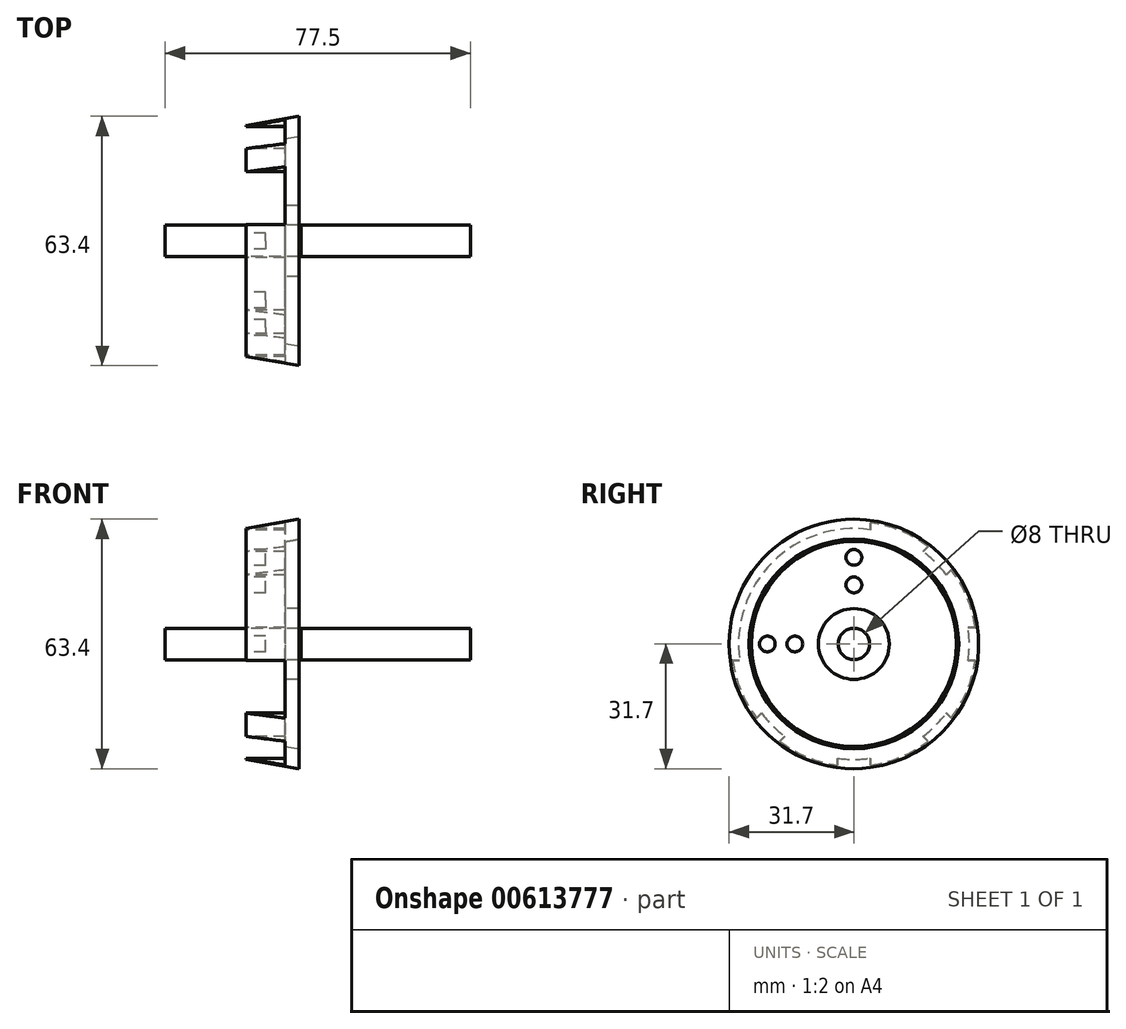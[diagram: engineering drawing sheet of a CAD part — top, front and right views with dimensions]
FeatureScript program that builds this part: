
annotation { "Feature Type Name" : "Feature", "Feature Type Description" : "" }
export const myFeature = defineFeature(function(context is Context, id is Id, definition is map)
    precondition{}
    {
        {
            var Q0;
            Q0=qCreatedBy(makeId("Front.planeOp"),FACE);
            var sketch = newSketch(context, id + "F0", { "sketchPlane" : qUnion([Q0])});
            skLineSegment(sketch, "E0", {"start": v(0, 0) * mm, "end": v(43, 0) * mm});
            skLineSegment(sketch, "E1", {"start": v(43, 0) * mm, "end": v(43, 14.5) * mm});
            skLineSegment(sketch, "E2", {"start": v(43, 14.5) * mm, "end": v(42, 14.5) * mm});
            skLineSegment(sketch, "E3", {"start": v(42, 14.5) * mm, "end": v(42, 31.7) * mm});
            skLineSegment(sketch, "E4", {"start": v(42, 31.7) * mm, "end": v(0, 31.7) * mm});
            skLineSegment(sketch, "E5", {"start": v(0, 31.7) * mm, "end": v(0, 0) * mm});
            skLineSegment(sketch, "E6", {"start": v(-0.5, 0) * mm, "end": v(-0.5, 31.7) * mm});
            skLineSegment(sketch, "E7", {"start": v(-0.5, 31.7) * mm, "end": v(-14, 29.32) * mm});
            skLineSegment(sketch, "E8", {"start": v(-14, 29.32) * mm, "end": v(-14, 0) * mm});
            skLineSegment(sketch, "E9", {"start": v(-14, 0) * mm, "end": v(-0.5, 0) * mm});
            skLineSegment(sketch, "E10", {"start": v(-34.5, 0) * mm, "end": v(43, 0) * mm});
            skLineSegment(sketch, "E11", {"start": v(-14, 29.32) * mm, "end": v(-14, 31.7) * mm});
            skLineSegment(sketch, "E12", {"start": v(-14, 31.7) * mm, "end": v(-0.5, 31.7) * mm});
            skLineSegment(sketch, "E13", {"start": v(-0.5, 31.7) * mm, "end": v(-0.5, 31.7) * mm});
            skLineSegment(sketch, "E14", {"start": v(-34.5, 0) * mm, "end": v(-34.5, 4) * mm});
            skLineSegment(sketch, "E15", {"start": v(-34.5, 4) * mm, "end": v(43, 4) * mm});
            skPoint(sketch, "E15.endSnap0", {"position": v(43, 7.25) * mm});
            skLineSegment(sketch, "E16", {"start": v(43, 4) * mm, "end": v(43, 0) * mm});
            skSolve(sketch);
        }
        {
            var Q0;
            {var subQ0=sQuery(id+"F0.wireOp",EDGE,"E7");Q0=makeQuery(id+"F0.imprint","IMPRINT",FACE,{"disambiguationData":[TD([[makeQuery(id+"F0.imprint","IMPRINT",EDGE,{"derivedFrom":subQ0}),1.0]])]});}
            var Q1;
            Q1=sQuery(id+"F0.wireOp",EDGE,"E10");
            revolve(context, id + "F1", {"entities" : qUnion([Q0]), "axis" : qUnion([Q1]), "revolveType" : RevolveType.FULL});
        }
        {
            var Q0;
            {var subQ1=sQuery(id+"F0.wireOp",EDGE,"E1");Q0=makeQuery(id+"F0.imprint","IMPRINT",FACE,{"disambiguationData":[TD([[makeQuery(id+"F0.imprint","IMPRINT",EDGE,{"derivedFrom":subQ1}),1.0]])]});}
            var Q1;
            {var subQ5=sQuery(id+"F0.wireOp",EDGE,"E14");Q1=makeQuery(id+"F0.imprint","IMPRINT",FACE,{"disambiguationData":[TD([[makeQuery(id+"F0.imprint","IMPRINT",EDGE,{"derivedFrom":subQ5}),-1.0]])]});}
            var Q2;
            {var subQ0=sQuery(id+"F0.wireOp",EDGE,"E10");var subQ1=sQuery(id+"F0.wireOp",EDGE,"E6");var subQ2=makeQuery(id+"F0.imprint","INTERSECT",VERTEX,{"derivedFrom":[subQ1,subQ0]});Q2=makeQuery(id+"F0.imprint","IMPRINT",FACE,{"disambiguationData":[TD([[makeQuery(id+"F0.imprint","IMPRINT",EDGE,{"disambiguationData":[TD([[subQ2,-1.0]])],"derivedFrom":subQ1}),1.0]])]});}
            var Q3;
            {var subQ5=sQuery(id+"F0.wireOp",EDGE,"E16");Q3=makeQuery(id+"F0.imprint","IMPRINT",FACE,{"disambiguationData":[TD([[makeQuery(id+"F0.imprint","IMPRINT",EDGE,{"derivedFrom":subQ5}),-1.0]])]});}
            var Q4;
            Q4=sQuery(id+"F0.wireOp",EDGE,"E10");
            revolve(context, id + "F2", {"entities" : qUnion([Q0, Q1, Q2, Q3]), "axis" : qUnion([Q4]), "revolveType" : RevolveType.FULL});
        }
        {
            var Q0;
            Q0=makeQuery(id+"F2.opRevolve","SWEPT_FACE",FACE,{"disambiguationData":[OSD([sQuery(id+"F0.wireOp",EDGE,"E1"),sQuery(id+"F0.wireOp",EDGE,"E16")])]});
            var sketch = newSketch(context, id + "F3", { "sketchPlane" : qUnion([Q0])});
            skCircle(sketch, "E17", {"center": v(0, 11) * mm, "radius": 2 * mm});
            skLineSegment(sketch, "E18", {"start": v(0, 31.85) * mm, "end": v(0, -39.83) * mm, "construction": true});
            skCircle(sketch, "E19.1.0", {"center": v(-11, 0) * mm, "radius": 2 * mm});
            skCircle(sketch, "E19.2.0", {"center": v(0, -11) * mm, "radius": 2 * mm});
            skCircle(sketch, "E19.3.0", {"center": v(11, 0) * mm, "radius": 2 * mm});
            skPoint(sketch, "E19.center", {"position": v(0, 0) * mm});
            skSolve(sketch);
        }
        {
            var Q0;
            Q0=makeQuery(id+"F3.imprint","IMPRINT",FACE,{"disambiguationData":[TD([[makeQuery(id+"F3.imprint","IMPRINT",EDGE,{"derivedFrom":sQuery(id+"F3.wireOp",EDGE,"E17")}),1.0]])]});
            var Q1;
            Q1=makeQuery(id+"F3.imprint","IMPRINT",FACE,{"disambiguationData":[TD([[makeQuery(id+"F3.imprint","IMPRINT",EDGE,{"derivedFrom":sQuery(id+"F3.wireOp",EDGE,"E19.1.0")}),1.0]])]});
            var Q2;
            Q2=makeQuery(id+"F3.imprint","IMPRINT",FACE,{"disambiguationData":[TD([[makeQuery(id+"F3.imprint","IMPRINT",EDGE,{"derivedFrom":sQuery(id+"F3.wireOp",EDGE,"E19.2.0")}),1.0]])]});
            var Q3;
            Q3=makeQuery(id+"F3.imprint","IMPRINT",FACE,{"disambiguationData":[TD([[makeQuery(id+"F3.imprint","IMPRINT",EDGE,{"derivedFrom":sQuery(id+"F3.wireOp",EDGE,"E19.3.0")}),1.0]])]});
            extrude(context, id + "F4", {"entities" : qUnion([Q0, Q1, Q2, Q3]), "operationType" : NewBodyOperationType.REMOVE, "oppositeDirection" : true, "depth" : 10 * mm, "offsetDistance" : 25 * mm});
        }
        {
            var Q0;
            Q0=makeQuery(id+"F1.opRevolve","SWEPT_FACE",FACE,{"disambiguationData":[OSD([sQuery(id+"F0.wireOp",EDGE,"E8")])]});
            var sketch = newSketch(context, id + "F5", { "sketchPlane" : qUnion([Q0])});
            skCircle(sketch, "E20", {"center": v(0, 0) * mm, "radius": 15 * mm});
            skCircle(sketch, "E21", {"center": v(0, 15) * mm, "radius": 2 * mm});
            skPoint(sketch, "E22.center.orphan", {"position": v(0, 22) * mm});
            skCircle(sketch, "E23", {"center": v(0, 0) * mm, "radius": 22 * mm});
            skCircle(sketch, "E24", {"center": v(0, 22) * mm, "radius": 2 * mm});
            skCircle(sketch, "E25.1.0", {"center": v(-22, 0) * mm, "radius": 2 * mm});
            skCircle(sketch, "E25.1.1", {"center": v(-15, 0) * mm, "radius": 2 * mm});
            skCircle(sketch, "E25.2.0", {"center": v(0, -22) * mm, "radius": 2 * mm});
            skCircle(sketch, "E25.2.1", {"center": v(0, -15) * mm, "radius": 2 * mm});
            skCircle(sketch, "E25.3.0", {"center": v(22, 0) * mm, "radius": 2 * mm});
            skCircle(sketch, "E25.3.1", {"center": v(15, 0) * mm, "radius": 2 * mm});
            skSolve(sketch);
        }
        {
            var Q0;
            Q0=makeQuery(id+"F1.opRevolve","SWEPT_FACE",FACE,{"disambiguationData":[OSD([sQuery(id+"F0.wireOp",EDGE,"E6")])]});
            shell(context, id + "F6", {"entities" : qUnion([Q0]), "thickness" : 5 * mm});
        }
        {
            var Q0;
            {var subQ0=sQuery(id+"F5.wireOp",EDGE,"E25.1.0");var subQ1=sQuery(id+"F5.wireOp",EDGE,"E23");var subQ2=makeQuery(id+"F5.imprint","INTERSECT",VERTEX,{"disambiguationData":[OD(0.0)],"derivedFrom":[subQ1,subQ0]});Q0=makeQuery(id+"F5.imprint","IMPRINT",FACE,{"disambiguationData":[TD([[makeQuery(id+"F5.imprint","IMPRINT",EDGE,{"disambiguationData":[TD([[subQ2,-1.0]])],"derivedFrom":subQ1}),-1.0]])]});}
            var Q1;
            {var subQ0=sQuery(id+"F5.wireOp",EDGE,"E25.1.0");var subQ1=sQuery(id+"F5.wireOp",EDGE,"E23");var subQ2=makeQuery(id+"F5.imprint","INTERSECT",VERTEX,{"disambiguationData":[OD(0.0)],"derivedFrom":[subQ1,subQ0]});Q1=makeQuery(id+"F5.imprint","IMPRINT",FACE,{"disambiguationData":[TD([[makeQuery(id+"F5.imprint","IMPRINT",EDGE,{"disambiguationData":[TD([[subQ2,-1.0]])],"derivedFrom":subQ1}),1.0]])]});}
            var Q2;
            {var subQ0=sQuery(id+"F5.wireOp",EDGE,"E25.1.1");var subQ1=sQuery(id+"F5.wireOp",EDGE,"E20");var subQ2=makeQuery(id+"F5.imprint","INTERSECT",VERTEX,{"disambiguationData":[OD(0.0)],"derivedFrom":[subQ1,subQ0]});Q2=makeQuery(id+"F5.imprint","IMPRINT",FACE,{"disambiguationData":[TD([[makeQuery(id+"F5.imprint","IMPRINT",EDGE,{"disambiguationData":[TD([[subQ2,-1.0]])],"derivedFrom":subQ1}),1.0]])]});}
            var Q3;
            {var subQ0=sQuery(id+"F5.wireOp",EDGE,"E25.1.1");var subQ1=sQuery(id+"F5.wireOp",EDGE,"E20");var subQ2=makeQuery(id+"F5.imprint","INTERSECT",VERTEX,{"disambiguationData":[OD(0.0)],"derivedFrom":[subQ1,subQ0]});Q3=makeQuery(id+"F5.imprint","IMPRINT",FACE,{"disambiguationData":[TD([[makeQuery(id+"F5.imprint","IMPRINT",EDGE,{"disambiguationData":[TD([[subQ2,-1.0]])],"derivedFrom":subQ1}),-1.0]])]});}
            var Q4;
            {var subQ0=sQuery(id+"F5.wireOp",EDGE,"E24");var subQ1=sQuery(id+"F5.wireOp",EDGE,"E23");var subQ2=makeQuery(id+"F5.imprint","INTERSECT",VERTEX,{"disambiguationData":[OD(0.0)],"derivedFrom":[subQ1,subQ0]});Q4=makeQuery(id+"F5.imprint","IMPRINT",FACE,{"disambiguationData":[TD([[makeQuery(id+"F5.imprint","IMPRINT",EDGE,{"disambiguationData":[TD([[subQ2,-1.0]])],"derivedFrom":subQ1}),1.0]])]});}
            var Q5;
            {var subQ0=sQuery(id+"F5.wireOp",EDGE,"E24");var subQ1=sQuery(id+"F5.wireOp",EDGE,"E23");var subQ2=makeQuery(id+"F5.imprint","INTERSECT",VERTEX,{"disambiguationData":[OD(0.0)],"derivedFrom":[subQ1,subQ0]});Q5=makeQuery(id+"F5.imprint","IMPRINT",FACE,{"disambiguationData":[TD([[makeQuery(id+"F5.imprint","IMPRINT",EDGE,{"disambiguationData":[TD([[subQ2,-1.0]])],"derivedFrom":subQ1}),-1.0]])]});}
            var Q6;
            {var subQ0=sQuery(id+"F5.wireOp",EDGE,"E21");var subQ1=sQuery(id+"F5.wireOp",EDGE,"E20");var subQ2=makeQuery(id+"F5.imprint","INTERSECT",VERTEX,{"disambiguationData":[OD(0.0)],"derivedFrom":[subQ1,subQ0]});Q6=makeQuery(id+"F5.imprint","IMPRINT",FACE,{"disambiguationData":[TD([[makeQuery(id+"F5.imprint","IMPRINT",EDGE,{"disambiguationData":[TD([[subQ2,-1.0]])],"derivedFrom":subQ1}),-1.0]])]});}
            var Q7;
            {var subQ0=sQuery(id+"F5.wireOp",EDGE,"E21");var subQ1=sQuery(id+"F5.wireOp",EDGE,"E20");var subQ2=makeQuery(id+"F5.imprint","INTERSECT",VERTEX,{"disambiguationData":[OD(0.0)],"derivedFrom":[subQ1,subQ0]});Q7=makeQuery(id+"F5.imprint","IMPRINT",FACE,{"disambiguationData":[TD([[makeQuery(id+"F5.imprint","IMPRINT",EDGE,{"disambiguationData":[TD([[subQ2,-1.0]])],"derivedFrom":subQ1}),1.0]])]});}
            var Q8;
            {var subQ0=sQuery(id+"F5.wireOp",EDGE,"E25.3.1");var subQ1=sQuery(id+"F5.wireOp",EDGE,"E20");var subQ2=makeQuery(id+"F5.imprint","INTERSECT",VERTEX,{"disambiguationData":[OD(0.0)],"derivedFrom":[subQ1,subQ0]});Q8=makeQuery(id+"F5.imprint","IMPRINT",FACE,{"disambiguationData":[TD([[makeQuery(id+"F5.imprint","IMPRINT",EDGE,{"disambiguationData":[TD([[subQ2,1.0]])],"derivedFrom":subQ1}),1.0]])]});}
            var Q9;
            {var subQ0=sQuery(id+"F5.wireOp",EDGE,"E25.3.1");var subQ1=sQuery(id+"F5.wireOp",EDGE,"E20");var subQ2=makeQuery(id+"F5.imprint","INTERSECT",VERTEX,{"disambiguationData":[OD(0.0)],"derivedFrom":[subQ1,subQ0]});Q9=makeQuery(id+"F5.imprint","IMPRINT",FACE,{"disambiguationData":[TD([[makeQuery(id+"F5.imprint","IMPRINT",EDGE,{"disambiguationData":[TD([[subQ2,1.0]])],"derivedFrom":subQ1}),-1.0]])]});}
            var Q10;
            {var subQ0=sQuery(id+"F5.wireOp",EDGE,"E25.3.0");var subQ1=sQuery(id+"F5.wireOp",EDGE,"E23");var subQ2=makeQuery(id+"F5.imprint","INTERSECT",VERTEX,{"disambiguationData":[OD(0.0)],"derivedFrom":[subQ1,subQ0]});Q10=makeQuery(id+"F5.imprint","IMPRINT",FACE,{"disambiguationData":[TD([[makeQuery(id+"F5.imprint","IMPRINT",EDGE,{"disambiguationData":[TD([[subQ2,1.0]])],"derivedFrom":subQ1}),1.0]])]});}
            var Q11;
            {var subQ0=sQuery(id+"F5.wireOp",EDGE,"E25.3.0");var subQ1=sQuery(id+"F5.wireOp",EDGE,"E23");var subQ2=makeQuery(id+"F5.imprint","INTERSECT",VERTEX,{"disambiguationData":[OD(0.0)],"derivedFrom":[subQ1,subQ0]});Q11=makeQuery(id+"F5.imprint","IMPRINT",FACE,{"disambiguationData":[TD([[makeQuery(id+"F5.imprint","IMPRINT",EDGE,{"disambiguationData":[TD([[subQ2,1.0]])],"derivedFrom":subQ1}),-1.0]])]});}
            var Q12;
            {var subQ0=sQuery(id+"F5.wireOp",EDGE,"E25.2.0");var subQ1=sQuery(id+"F5.wireOp",EDGE,"E23");var subQ2=makeQuery(id+"F5.imprint","INTERSECT",VERTEX,{"disambiguationData":[OD(0.0)],"derivedFrom":[subQ1,subQ0]});Q12=makeQuery(id+"F5.imprint","IMPRINT",FACE,{"disambiguationData":[TD([[makeQuery(id+"F5.imprint","IMPRINT",EDGE,{"disambiguationData":[TD([[subQ2,-1.0]])],"derivedFrom":subQ1}),1.0]])]});}
            var Q13;
            {var subQ0=sQuery(id+"F5.wireOp",EDGE,"E25.2.1");var subQ1=sQuery(id+"F5.wireOp",EDGE,"E20");var subQ2=makeQuery(id+"F5.imprint","INTERSECT",VERTEX,{"disambiguationData":[OD(0.0)],"derivedFrom":[subQ1,subQ0]});Q13=makeQuery(id+"F5.imprint","IMPRINT",FACE,{"disambiguationData":[TD([[makeQuery(id+"F5.imprint","IMPRINT",EDGE,{"disambiguationData":[TD([[subQ2,-1.0]])],"derivedFrom":subQ1}),-1.0]])]});}
            var Q14;
            {var subQ0=sQuery(id+"F5.wireOp",EDGE,"E25.2.1");var subQ1=sQuery(id+"F5.wireOp",EDGE,"E20");var subQ2=makeQuery(id+"F5.imprint","INTERSECT",VERTEX,{"disambiguationData":[OD(0.0)],"derivedFrom":[subQ1,subQ0]});Q14=makeQuery(id+"F5.imprint","IMPRINT",FACE,{"disambiguationData":[TD([[makeQuery(id+"F5.imprint","IMPRINT",EDGE,{"disambiguationData":[TD([[subQ2,-1.0]])],"derivedFrom":subQ1}),1.0]])]});}
            var Q15;
            {var subQ0=sQuery(id+"F5.wireOp",EDGE,"E25.2.0");var subQ1=sQuery(id+"F5.wireOp",EDGE,"E23");var subQ2=makeQuery(id+"F5.imprint","INTERSECT",VERTEX,{"disambiguationData":[OD(0.0)],"derivedFrom":[subQ1,subQ0]});Q15=makeQuery(id+"F5.imprint","IMPRINT",FACE,{"disambiguationData":[TD([[makeQuery(id+"F5.imprint","IMPRINT",EDGE,{"disambiguationData":[TD([[subQ2,-1.0]])],"derivedFrom":subQ1}),-1.0]])]});}
            extrude(context, id + "F7", {"entities" : qUnion([Q0, Q1, Q2, Q3, Q4, Q5, Q6, Q7, Q8, Q9, Q10, Q11, Q12, Q13, Q14, Q15]), "operationType" : NewBodyOperationType.REMOVE, "oppositeDirection" : true, "depth" : 10 * mm, "offsetDistance" : 25 * mm});
        }
        {
            var Q0;
            Q0=makeQuery(id+"F1.opRevolve","SWEPT_FACE",FACE,{"disambiguationData":[OSD([sQuery(id+"F0.wireOp",EDGE,"E8")])]});
            var sketch = newSketch(context, id + "F8", { "sketchPlane" : qUnion([Q0])});
            skLineSegment(sketch, "E26", {"start": v(0, 0) * mm, "end": v(-34.52, 34.52) * mm, "construction": true});
            skLineSegment(sketch, "E27", {"start": v(0, 0) * mm, "end": v(-20.27, 48.94) * mm, "construction": true});
            skCircle(sketch, "E28", {"center": v(0, 0) * mm, "radius": 18.5 * mm, "construction": true});
            skPoint(sketch, "E29", {"position": v(-7.08, 17.08) * mm});
            skArc(sketch, "E30", {"start": v(-9.8, 15.68) * mm, "mid": v(-5.9, 14.26) * mm, "end": v(-4.17, 18.02) * mm});
            skLineSegment(sketch, "E31", {"start": v(-2, 15.01) * mm, "end": v(-1.95, 22.45) * mm, "construction": true});
            skLineSegment(sketch, "E32", {"start": v(-4.17, 18.02) * mm, "end": v(-4.17, 29.02) * mm});
            skLineSegment(sketch, "E33.MirrorCS", {"start": v(-9.8, 15.68) * mm, "end": v(-17.58, 23.47) * mm});
            skLineSegment(sketch, "E34", {"start": v(-4.17, 18.02) * mm, "end": v(-4.17, 40.77) * mm});
            skLineSegment(sketch, "E35", {"start": v(-4.17, 40.77) * mm, "end": v(-15.02, 36.27) * mm});
            skLineSegment(sketch, "E36.MirrorCS", {"start": v(-9.8, 15.68) * mm, "end": v(-25.88, 31.77) * mm});
            skLineSegment(sketch, "E37.MirrorCS", {"start": v(-25.88, 31.77) * mm, "end": v(-15.02, 36.27) * mm});
            skLineSegment(sketch, "E38.1.0", {"start": v(-40.77, 4.17) * mm, "end": v(-36.27, 15.02) * mm});
            skLineSegment(sketch, "E38.1.1", {"start": v(-31.77, 25.88) * mm, "end": v(-36.27, 15.02) * mm});
            skLineSegment(sketch, "E38.1.2", {"start": v(0, 0) * mm, "end": v(-48.94, 20.27) * mm, "construction": true});
            skLineSegment(sketch, "E38.1.3", {"start": v(-18.02, 4.17) * mm, "end": v(-40.77, 4.17) * mm});
            skLineSegment(sketch, "E38.1.4", {"start": v(-15.68, 9.8) * mm, "end": v(-31.77, 25.88) * mm});
            skArc(sketch, "E38.1.5", {"start": v(-18.02, 4.17) * mm, "mid": v(-14.26, 5.9) * mm, "end": v(-15.68, 9.8) * mm});
            skLineSegment(sketch, "E38.2.0", {"start": v(-31.77, -25.88) * mm, "end": v(-36.27, -15.02) * mm});
            skLineSegment(sketch, "E38.2.1", {"start": v(-40.77, -4.17) * mm, "end": v(-36.27, -15.02) * mm});
            skLineSegment(sketch, "E38.2.2", {"start": v(0, 0) * mm, "end": v(-48.94, -20.27) * mm, "construction": true});
            skLineSegment(sketch, "E38.2.3", {"start": v(-15.68, -9.8) * mm, "end": v(-31.77, -25.88) * mm});
            skLineSegment(sketch, "E38.2.4", {"start": v(-18.02, -4.17) * mm, "end": v(-40.77, -4.17) * mm});
            skArc(sketch, "E38.2.5", {"start": v(-15.68, -9.8) * mm, "mid": v(-14.26, -5.9) * mm, "end": v(-18.02, -4.17) * mm});
            skLineSegment(sketch, "E38.3.0", {"start": v(-4.17, -40.77) * mm, "end": v(-15.02, -36.27) * mm});
            skLineSegment(sketch, "E38.3.1", {"start": v(-25.88, -31.77) * mm, "end": v(-15.02, -36.27) * mm});
            skLineSegment(sketch, "E38.3.2", {"start": v(0, 0) * mm, "end": v(-20.27, -48.94) * mm, "construction": true});
            skLineSegment(sketch, "E38.3.3", {"start": v(-4.17, -18.02) * mm, "end": v(-4.17, -40.77) * mm});
            skLineSegment(sketch, "E38.3.4", {"start": v(-9.8, -15.68) * mm, "end": v(-25.88, -31.77) * mm});
            skArc(sketch, "E38.3.5", {"start": v(-4.17, -18.02) * mm, "mid": v(-5.9, -14.26) * mm, "end": v(-9.8, -15.68) * mm});
            skLineSegment(sketch, "E38.4.0", {"start": v(25.88, -31.77) * mm, "end": v(15.02, -36.27) * mm});
            skLineSegment(sketch, "E38.4.1", {"start": v(4.17, -40.77) * mm, "end": v(15.02, -36.27) * mm});
            skLineSegment(sketch, "E38.4.2", {"start": v(0, 0) * mm, "end": v(20.27, -48.94) * mm, "construction": true});
            skLineSegment(sketch, "E38.4.3", {"start": v(9.8, -15.68) * mm, "end": v(25.88, -31.77) * mm});
            skLineSegment(sketch, "E38.4.4", {"start": v(4.17, -18.02) * mm, "end": v(4.17, -40.77) * mm});
            skArc(sketch, "E38.4.5", {"start": v(9.8, -15.68) * mm, "mid": v(5.9, -14.26) * mm, "end": v(4.17, -18.02) * mm});
            skLineSegment(sketch, "E38.5.0", {"start": v(40.77, -4.17) * mm, "end": v(36.27, -15.02) * mm});
            skLineSegment(sketch, "E38.5.1", {"start": v(31.77, -25.88) * mm, "end": v(36.27, -15.02) * mm});
            skLineSegment(sketch, "E38.5.2", {"start": v(0, 0) * mm, "end": v(48.94, -20.27) * mm, "construction": true});
            skLineSegment(sketch, "E38.5.3", {"start": v(18.02, -4.17) * mm, "end": v(40.77, -4.17) * mm});
            skLineSegment(sketch, "E38.5.4", {"start": v(15.68, -9.8) * mm, "end": v(31.77, -25.88) * mm});
            skArc(sketch, "E38.5.5", {"start": v(18.02, -4.17) * mm, "mid": v(14.26, -5.9) * mm, "end": v(15.68, -9.8) * mm});
            skLineSegment(sketch, "E38.6.0", {"start": v(31.77, 25.88) * mm, "end": v(36.27, 15.02) * mm});
            skLineSegment(sketch, "E38.6.1", {"start": v(40.77, 4.17) * mm, "end": v(36.27, 15.02) * mm});
            skLineSegment(sketch, "E38.6.2", {"start": v(0, 0) * mm, "end": v(48.94, 20.27) * mm, "construction": true});
            skLineSegment(sketch, "E38.6.3", {"start": v(15.68, 9.8) * mm, "end": v(31.77, 25.88) * mm});
            skLineSegment(sketch, "E38.6.4", {"start": v(18.02, 4.17) * mm, "end": v(40.77, 4.17) * mm});
            skArc(sketch, "E38.6.5", {"start": v(15.68, 9.8) * mm, "mid": v(14.26, 5.9) * mm, "end": v(18.02, 4.17) * mm});
            skLineSegment(sketch, "E38.7.0", {"start": v(4.17, 40.77) * mm, "end": v(15.02, 36.27) * mm});
            skLineSegment(sketch, "E38.7.1", {"start": v(25.88, 31.77) * mm, "end": v(15.02, 36.27) * mm});
            skLineSegment(sketch, "E38.7.2", {"start": v(0, 0) * mm, "end": v(20.27, 48.94) * mm, "construction": true});
            skLineSegment(sketch, "E38.7.3", {"start": v(4.17, 18.02) * mm, "end": v(4.17, 40.77) * mm});
            skLineSegment(sketch, "E38.7.4", {"start": v(9.8, 15.68) * mm, "end": v(25.88, 31.77) * mm});
            skArc(sketch, "E38.7.5", {"start": v(4.17, 18.02) * mm, "mid": v(5.9, 14.26) * mm, "end": v(9.8, 15.68) * mm});
            skSolve(sketch);
        }
        {
            var Q0;
            Q0=makeQuery(id+"F8.imprint","IMPRINT",FACE,{"disambiguationData":[TD([[makeQuery(id+"F8.imprint","IMPRINT",EDGE,{"derivedFrom":sQuery(id+"F8.wireOp",EDGE,"E30")}),1.0]])]});
            var Q1;
            {var subQ6=sQuery(id+"F8.wireOp",EDGE,"E35");Q1=makeQuery(id+"F8.imprint","IMPRINT",FACE,{"disambiguationData":[TD([[makeQuery(id+"F8.imprint","IMPRINT",EDGE,{"derivedFrom":subQ6}),1.0]])]});}
            var Q2;
            {var subQ1=sQuery(id+"F8.wireOp",EDGE,"E38.1.0");Q2=makeQuery(id+"F8.imprint","IMPRINT",FACE,{"disambiguationData":[TD([[makeQuery(id+"F8.imprint","IMPRINT",EDGE,{"derivedFrom":subQ1}),-1.0]])]});}
            var Q3;
            {var subQ0=sQuery(id+"F8.wireOp",EDGE,"E38.1.5");Q3=makeQuery(id+"F8.imprint","IMPRINT",FACE,{"disambiguationData":[TD([[makeQuery(id+"F8.imprint","IMPRINT",EDGE,{"derivedFrom":subQ0}),1.0]])]});}
            var Q4;
            {var subQ1=sQuery(id+"F8.wireOp",EDGE,"E38.2.0");Q4=makeQuery(id+"F8.imprint","IMPRINT",FACE,{"disambiguationData":[TD([[makeQuery(id+"F8.imprint","IMPRINT",EDGE,{"derivedFrom":subQ1}),-1.0]])]});}
            var Q5;
            {var subQ0=sQuery(id+"F8.wireOp",EDGE,"E38.2.5");Q5=makeQuery(id+"F8.imprint","IMPRINT",FACE,{"disambiguationData":[TD([[makeQuery(id+"F8.imprint","IMPRINT",EDGE,{"derivedFrom":subQ0}),1.0]])]});}
            var Q6;
            {var subQ1=sQuery(id+"F8.wireOp",EDGE,"E38.3.0");Q6=makeQuery(id+"F8.imprint","IMPRINT",FACE,{"disambiguationData":[TD([[makeQuery(id+"F8.imprint","IMPRINT",EDGE,{"derivedFrom":subQ1}),-1.0]])]});}
            var Q7;
            {var subQ0=sQuery(id+"F8.wireOp",EDGE,"E38.3.5");Q7=makeQuery(id+"F8.imprint","IMPRINT",FACE,{"disambiguationData":[TD([[makeQuery(id+"F8.imprint","IMPRINT",EDGE,{"derivedFrom":subQ0}),1.0]])]});}
            var Q8;
            {var subQ1=sQuery(id+"F8.wireOp",EDGE,"E38.4.0");Q8=makeQuery(id+"F8.imprint","IMPRINT",FACE,{"disambiguationData":[TD([[makeQuery(id+"F8.imprint","IMPRINT",EDGE,{"derivedFrom":subQ1}),-1.0]])]});}
            var Q9;
            {var subQ0=sQuery(id+"F8.wireOp",EDGE,"E38.4.5");Q9=makeQuery(id+"F8.imprint","IMPRINT",FACE,{"disambiguationData":[TD([[makeQuery(id+"F8.imprint","IMPRINT",EDGE,{"derivedFrom":subQ0}),1.0]])]});}
            var Q10;
            {var subQ1=sQuery(id+"F8.wireOp",EDGE,"E38.5.0");Q10=makeQuery(id+"F8.imprint","IMPRINT",FACE,{"disambiguationData":[TD([[makeQuery(id+"F8.imprint","IMPRINT",EDGE,{"derivedFrom":subQ1}),-1.0]])]});}
            var Q11;
            {var subQ0=sQuery(id+"F8.wireOp",EDGE,"E38.5.5");Q11=makeQuery(id+"F8.imprint","IMPRINT",FACE,{"disambiguationData":[TD([[makeQuery(id+"F8.imprint","IMPRINT",EDGE,{"derivedFrom":subQ0}),1.0]])]});}
            extrude(context, id + "F9", {"entities" : qUnion([Q0, Q1, Q2, Q3, Q4, Q5, Q6, Q7, Q8, Q9, Q10, Q11]), "operationType" : NewBodyOperationType.REMOVE, "oppositeDirection" : true, "depth" : 10 * mm, "offsetDistance" : 25 * mm});
        }
    });
